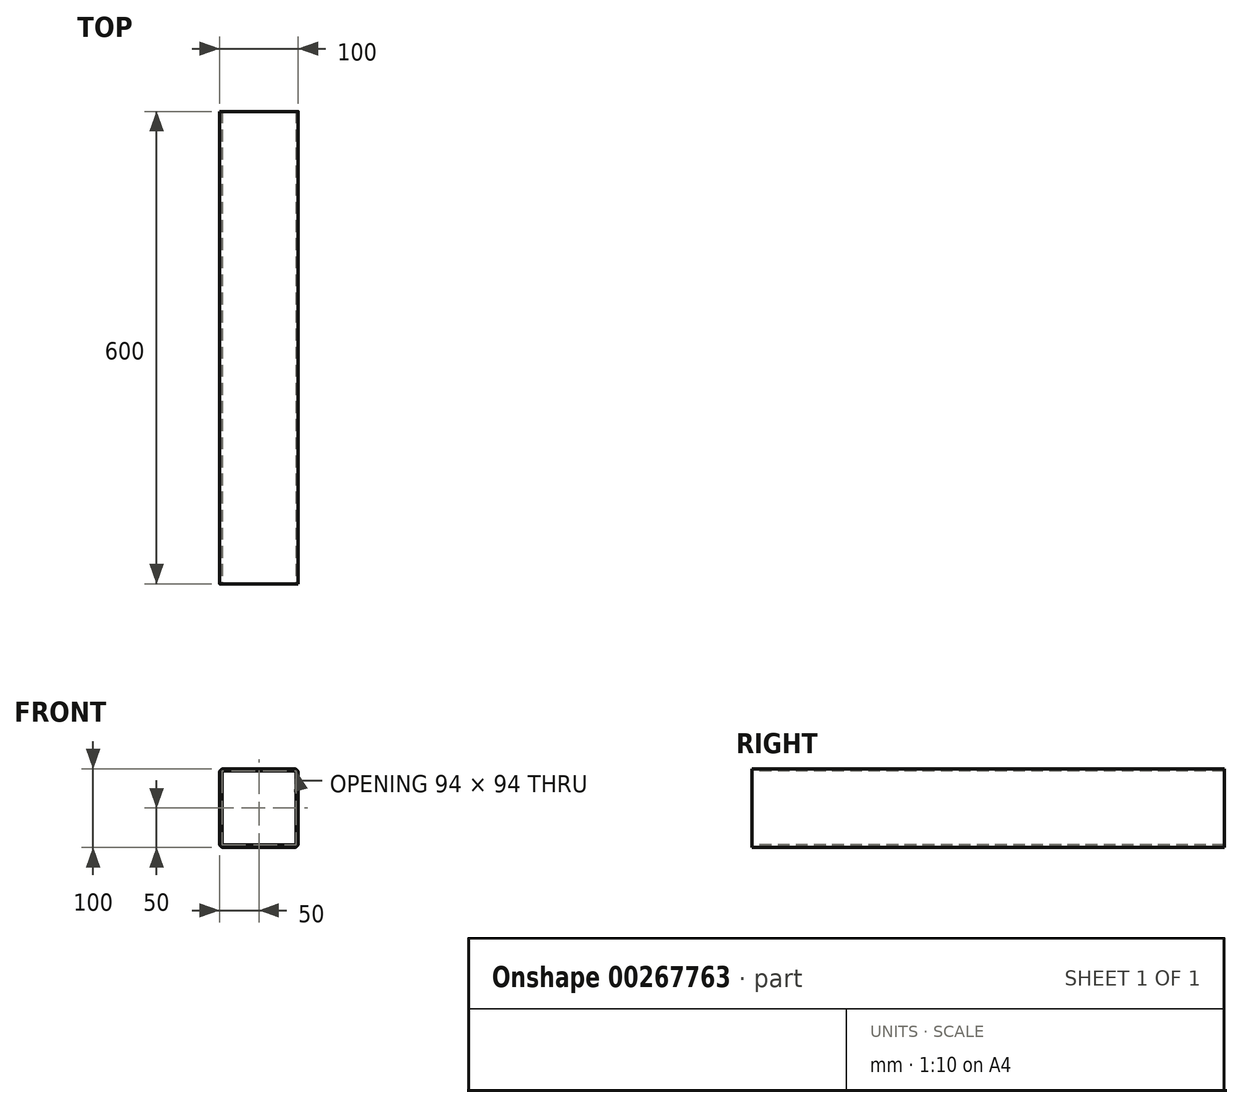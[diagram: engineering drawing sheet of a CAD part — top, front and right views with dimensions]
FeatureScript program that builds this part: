
annotation { "Feature Type Name" : "Feature", "Feature Type Description" : "" }
export const myFeature = defineFeature(function(context is Context, id is Id, definition is map)
    precondition{}
    {
        {
            var Q0;
            Q0=qCreatedBy(makeId("Front.planeOp"),FACE);
            var sketch = newSketch(context, id + "F0", { "sketchPlane" : qUnion([Q0])});
            skLineSegment(sketch, "E0.bottom", {"start": v(45, 50) * mm, "end": v(-45, 50) * mm});
            skLineSegment(sketch, "E0.top", {"start": v(45, -50) * mm, "end": v(-45, -50) * mm});
            skLineSegment(sketch, "E0.left", {"start": v(50, 45) * mm, "end": v(50, -45) * mm});
            skLineSegment(sketch, "E0.right", {"start": v(-50, 45) * mm, "end": v(-50, -45) * mm});
            skPoint(sketch, "E0.middle", {"position": v(0, 0) * mm});
            skPoint(sketch, "E1.visualSharp", {"position": v(-50, 50) * mm});
            skArc(sketch, "E1.filletArc", {"start": v(-45, 50) * mm, "mid": v(-48.54, 48.54) * mm, "end": v(-50, 45) * mm});
            skPoint(sketch, "E2.visualSharp", {"position": v(50, 50) * mm});
            skArc(sketch, "E2.filletArc", {"start": v(50, 45) * mm, "mid": v(48.54, 48.54) * mm, "end": v(45, 50) * mm});
            skPoint(sketch, "E3.visualSharp", {"position": v(50, -50) * mm});
            skArc(sketch, "E3.filletArc", {"start": v(45, -50) * mm, "mid": v(48.54, -48.54) * mm, "end": v(50, -45) * mm});
            skPoint(sketch, "E4.visualSharp", {"position": v(-50, -50) * mm});
            skArc(sketch, "E4.filletArc", {"start": v(-50, -45) * mm, "mid": v(-48.54, -48.54) * mm, "end": v(-45, -50) * mm});
            skArc(sketch, "E5.0", {"start": v(-45, 47) * mm, "mid": v(-46.41, 46.41) * mm, "end": v(-47, 45) * mm});
            skLineSegment(sketch, "E5.1", {"start": v(45, 47) * mm, "end": v(-45, 47) * mm});
            skLineSegment(sketch, "E5.2", {"start": v(-47, 45) * mm, "end": v(-47, -45) * mm});
            skArc(sketch, "E5.3", {"start": v(47, 45) * mm, "mid": v(46.41, 46.41) * mm, "end": v(45, 47) * mm});
            skArc(sketch, "E5.4", {"start": v(-47, -45) * mm, "mid": v(-46.41, -46.41) * mm, "end": v(-45, -47) * mm});
            skLineSegment(sketch, "E5.5", {"start": v(45, -47) * mm, "end": v(-45, -47) * mm});
            skArc(sketch, "E5.6", {"start": v(45, -47) * mm, "mid": v(46.41, -46.41) * mm, "end": v(47, -45) * mm});
            skLineSegment(sketch, "E5.7", {"start": v(47, 45) * mm, "end": v(47, -45) * mm});
            skSolve(sketch);
        }
        {
            var Q0;
            Q0=makeQuery(id+"F0.imprint","IMPRINT",FACE,{"disambiguationData":[TD([[makeQuery(id+"F0.imprint","IMPRINT",EDGE,{"derivedFrom":sQuery(id+"F0.wireOp",EDGE,"E0.bottom")}),1.0]])]});
            extrude(context, id + "F1", {"entities" : qUnion([Q0]), "oppositeDirection" : true, "depth" : 600 * mm});
        }
    });
